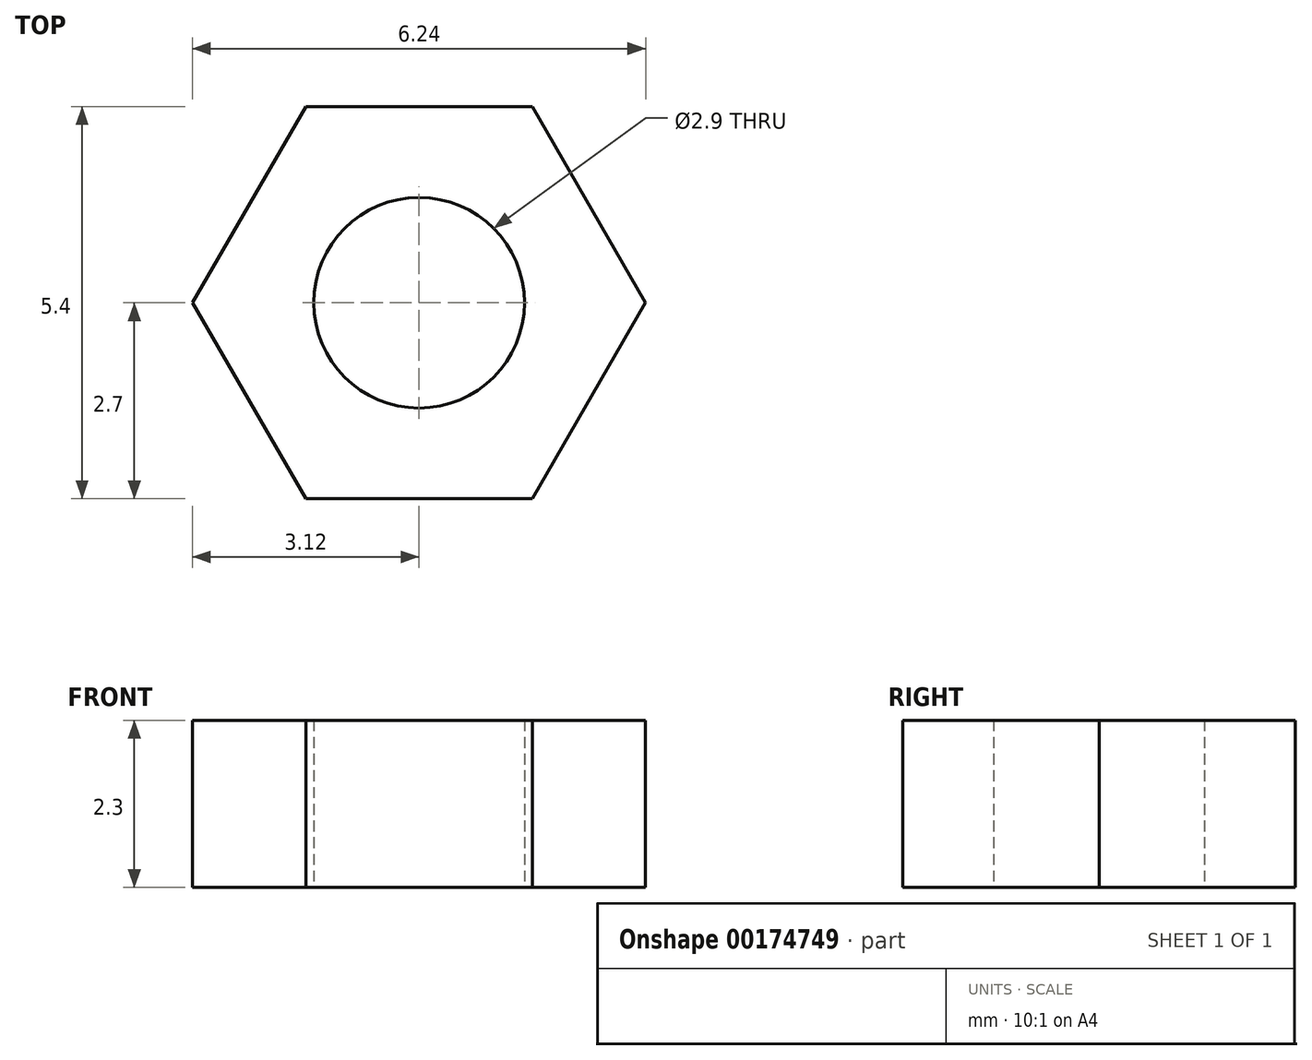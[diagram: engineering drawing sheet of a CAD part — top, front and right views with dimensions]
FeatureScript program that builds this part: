
annotation { "Feature Type Name" : "Feature", "Feature Type Description" : "" }
export const myFeature = defineFeature(function(context is Context, id is Id, definition is map)
    precondition{}
    {
        {
            var Q0;
            Q0=qCreatedBy(makeId("Top.planeOp"),FACE);
            var sketch = newSketch(context, id + "F0", { "sketchPlane" : qUnion([Q0])});
            skCircle(sketch, "E0.cCircle", {"center": v(0, 0) * mm, "radius": 2.7 * mm, "construction": true});
            skLineSegment(sketch, "E0.0", {"start": v(-1.56, 2.7) * mm, "end": v(1.56, 2.7) * mm});
            skLineSegment(sketch, "E0.1", {"start": v(1.56, 2.7) * mm, "end": v(3.12, 0) * mm});
            skLineSegment(sketch, "E0.2", {"start": v(3.12, 0) * mm, "end": v(1.56, -2.7) * mm});
            skLineSegment(sketch, "E0.3", {"start": v(1.56, -2.7) * mm, "end": v(-1.56, -2.7) * mm});
            skLineSegment(sketch, "E0.4", {"start": v(-1.56, -2.7) * mm, "end": v(-3.12, 0) * mm});
            skLineSegment(sketch, "E0.5", {"start": v(-3.12, 0) * mm, "end": v(-1.56, 2.7) * mm});
            skPoint(sketch, "E0.0.midPoint", {"position": v(0, 2.7) * mm});
            skCircle(sketch, "E1", {"center": v(0, 0) * mm, "radius": 1.45 * mm});
            skSolve(sketch);
        }
        {
            var Q0;
            Q0 = qSketchRegion(id + "F0", true);
            extrude(context, id + "F1", {"entities" : qUnion([Q0]), "depth" : 2.3 * mm});
        }
    });
